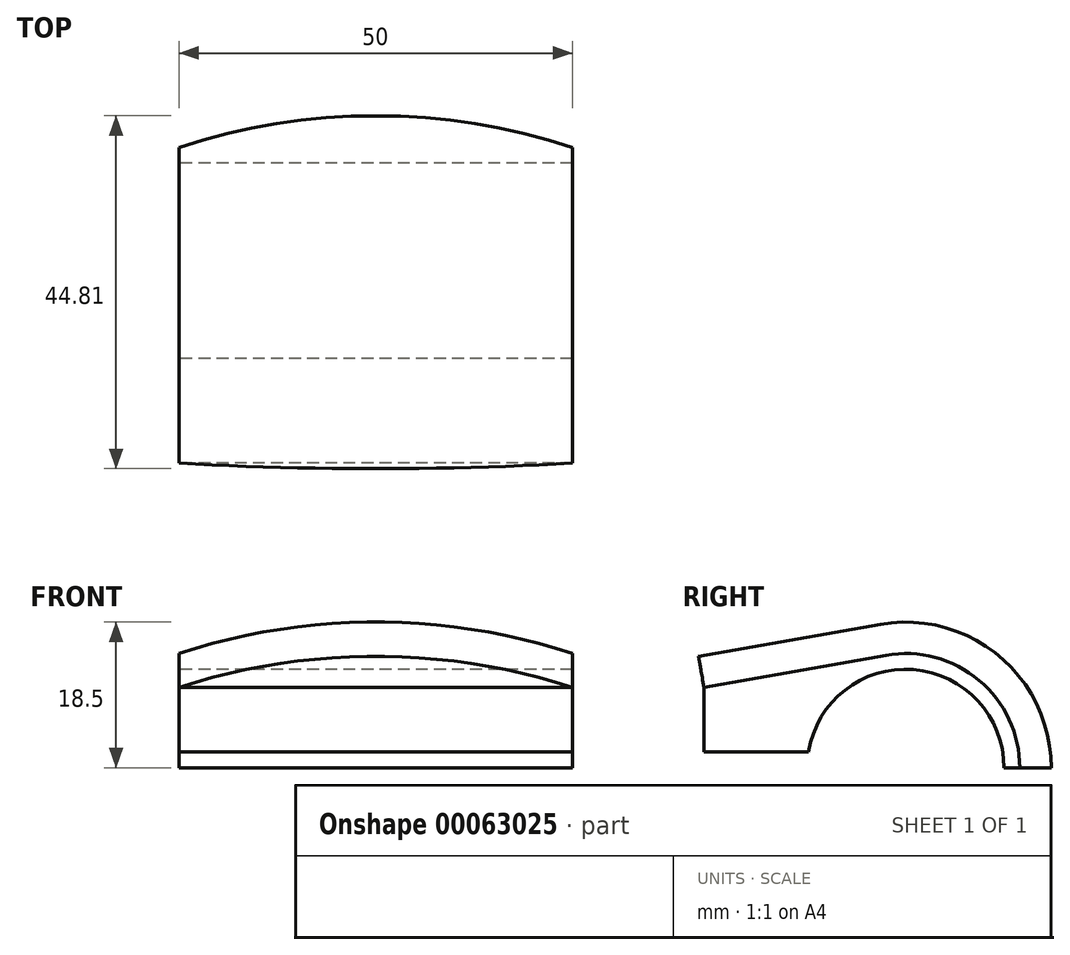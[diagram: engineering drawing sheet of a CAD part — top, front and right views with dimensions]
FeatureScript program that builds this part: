
annotation { "Feature Type Name" : "Feature", "Feature Type Description" : "" }
export const myFeature = defineFeature(function(context is Context, id is Id, definition is map)
    precondition{}
    {
        {
            var Q0;
            Q0=qCreatedBy(makeId("Top.planeOp"),FACE);
            var sketch = newSketch(context, id + "F0", { "sketchPlane" : qUnion([Q0])});
            skLineSegment(sketch, "E0", {"start": v(0, -18) * mm, "end": v(0, 18) * mm, "construction": true});
            skLineSegment(sketch, "E1", {"start": v(-20.94, 0) * mm, "end": v(20.94, 0) * mm, "construction": true});
            skLineSegment(sketch, "E2", {"start": v(-23.58, -3.08) * mm, "end": v(-2.65, -21.08) * mm});
            skLineSegment(sketch, "E3", {"start": v(2.65, -21.08) * mm, "end": v(23.58, -3.08) * mm});
            skLineSegment(sketch, "E4", {"start": v(-23.58, 3.08) * mm, "end": v(-2.65, 21.08) * mm});
            skLineSegment(sketch, "E5", {"start": v(2.65, 21.08) * mm, "end": v(23.58, 3.08) * mm});
            skLineSegment(sketch, "E6.bottom", {"start": v(-25, -22.06) * mm, "end": v(25, -22.06) * mm});
            skLineSegment(sketch, "E6.top", {"start": v(-25, 22.06) * mm, "end": v(25, 22.06) * mm, "construction": true});
            skLineSegment(sketch, "E6.left", {"start": v(-25, -22.06) * mm, "end": v(-25, 22.06) * mm});
            skLineSegment(sketch, "E6.right", {"start": v(25, -22.06) * mm, "end": v(25, 22.06) * mm});
            skArc(sketch, "E7", {"start": v(25, 18.06) * mm, "mid": v(0, 22.06) * mm, "end": v(-25, 18.06) * mm});
            skArc(sketch, "E8", {"start": v(0, 13.93) * mm, "mid": v(3.81, 16.58) * mm, "end": v(2.65, 21.08) * mm});
            skArc(sketch, "E9", {"start": v(-2.65, 21.08) * mm, "mid": v(-3.81, 16.58) * mm, "end": v(0, 13.93) * mm});
            skArc(sketch, "E10", {"start": v(2.65, 21.08) * mm, "mid": v(0, 22.06) * mm, "end": v(-2.65, 21.08) * mm});
            skArc(sketch, "E11", {"start": v(-23.58, 3.08) * mm, "mid": v(-25, 0) * mm, "end": v(-23.58, -3.08) * mm});
            skArc(sketch, "E12", {"start": v(-23.58, -3.08) * mm, "mid": v(-16.87, 0) * mm, "end": v(-23.58, 3.08) * mm});
            skArc(sketch, "E13", {"start": v(-2.65, -21.08) * mm, "mid": v(0, -22.06) * mm, "end": v(2.65, -21.08) * mm});
            skArc(sketch, "E14", {"start": v(2.65, -21.08) * mm, "mid": v(0, -13.93) * mm, "end": v(-2.65, -21.08) * mm});
            skArc(sketch, "E15", {"start": v(23.58, -3.08) * mm, "mid": v(25, 0) * mm, "end": v(23.58, 3.08) * mm});
            skArc(sketch, "E16", {"start": v(23.58, 3.08) * mm, "mid": v(16.87, 0) * mm, "end": v(23.58, -3.08) * mm});
            skSolve(sketch);
        }
        {
            var Q0;
            {var subQ0=sQuery(id+"F0.wireOp",EDGE,"E2");Q0=makeQuery(id+"F0.imprint","IMPRINT",FACE,{"disambiguationData":[TD([[makeQuery(id+"F0.imprint","IMPRINT",EDGE,{"derivedFrom":subQ0}),1.0]])]});}
            cPlane(context, id + "F1", {"entities" : qUnion([Q0]), "cplaneType" : CPlaneType.OFFSET, "offset" : 29 * mm, "width" : 150 * mm, "height" : 150 * mm});
        }
        {
            var Q0;
            Q0=qCreatedBy(id+"F1.planeOp",FACE);
            var sketch = newSketch(context, id + "F2", { "sketchPlane" : qUnion([Q0])});
            skLineSegment(sketch, "E17.bottom", {"start": v(-25, 22.06) * mm, "end": v(25, 22.06) * mm});
            skLineSegment(sketch, "E17.top", {"start": v(-25, -22.06) * mm, "end": v(25, -22.06) * mm});
            skLineSegment(sketch, "E17.left", {"start": v(-25, 22.06) * mm, "end": v(-25, -22.06) * mm});
            skLineSegment(sketch, "E17.right", {"start": v(25, 22.06) * mm, "end": v(25, -22.06) * mm});
            skArc(sketch, "E18", {"start": v(25, 18.06) * mm, "mid": v(0, 22.06) * mm, "end": v(-25, 18.06) * mm});
            skLineSegment(sketch, "E19", {"start": v(25, 18.06) * mm, "end": v(-25, 18.06) * mm});
            skSolve(sketch);
        }
        {
            var Q0;
            Q0=sQuery(id+"F2.wireOp",VERTEX,"E18.end");
            var Q1;
            Q1=sQuery(id+"F2.wireOp",VERTEX,"E17.left.end");
            var Q2;
            Q2=sQuery(id+"F0.wireOp",VERTEX,"E6.bottom.start");
            cPlane(context, id + "F3", {"entities" : qUnion([Q0, Q1, Q2]), "cplaneType" : CPlaneType.THREE_POINT, "offset" : 150 * mm, "width" : 150 * mm, "height" : 150 * mm});
        }
        {
            var Q0;
            Q0=qCreatedBy(id+"F3.planeOp",FACE);
            var sketch = newSketch(context, id + "F4", { "sketchPlane" : qUnion([Q0])});
            skCircle(sketch, "E20", {"center": v(-3.56, 29) * mm, "radius": 14.5 * mm});
            skCircle(sketch, "E21", {"center": v(-3.56, 29) * mm, "radius": 12.5 * mm});
            skLineSegment(sketch, "E22", {"start": v(22.06, 39.2) * mm, "end": v(22.06, 31) * mm});
            skLineSegment(sketch, "E23", {"start": v(22.06, 31) * mm, "end": v(8.78, 31) * mm});
            skLineSegment(sketch, "E24", {"start": v(-1.04, 43.28) * mm, "end": v(22.06, 39.2) * mm});
            skLineSegment(sketch, "E25", {"start": v(22.06, 29) * mm, "end": v(-22.06, 29) * mm});
            skSolve(sketch);
        }
        {
            var Q0;
            {var subQ4=sQuery(id+"F4.wireOp",EDGE,"E22");Q0=makeQuery(id+"F4.imprint","IMPRINT",FACE,{"disambiguationData":[TD([[makeQuery(id+"F4.imprint","IMPRINT",EDGE,{"derivedFrom":subQ4}),-1.0]])]});}
            var Q1;
            {var subQ3=sQuery(id+"F4.wireOp",EDGE,"E20");var subQ5=makeQuery(id+"F4.imprint","INTERSECT",VERTEX,{"derivedFrom":[subQ3,sQuery(id+"F4.wireOp",EDGE,"E24")]});Q1=makeQuery(id+"F4.imprint","IMPRINT",FACE,{"disambiguationData":[TD([[makeQuery(id+"F4.imprint","IMPRINT",EDGE,{"disambiguationData":[TD([[subQ5,1.0]])],"derivedFrom":subQ3}),1.0]])]});}
            extrude(context, id + "F5", {"entities" : qUnion([Q0, Q1]), "oppositeDirection" : true, "depth" : 50 * mm});
        }
        {
            var Q0;
            {var subQ0=sQuery(id+"F2.wireOp",EDGE,"E19");Q0=makeQuery(id+"F2.imprint","IMPRINT",FACE,{"disambiguationData":[TD([[makeQuery(id+"F2.imprint","IMPRINT",EDGE,{"derivedFrom":subQ0}),-1.0]])]});}
            var Q1;
            Q1=makeQuery(id+"F5.opExtrude","CAP_EDGE",EDGE,{"disambiguationData":[OSD([sQuery(id+"F4.wireOp",EDGE,"E20")])],"isStart":false});
            var Q2;
            Q2=makeQuery(id+"F5.opExtrude","CAP_EDGE",EDGE,{"disambiguationData":[OSD([sQuery(id+"F4.wireOp",EDGE,"E24")])],"isStart":false});
            sweep(context, id + "F6", {"operationType" : NewBodyOperationType.ADD, "profiles" : qUnion([Q0]), "path" : qUnion([Q1, Q2])});
        }
    });
